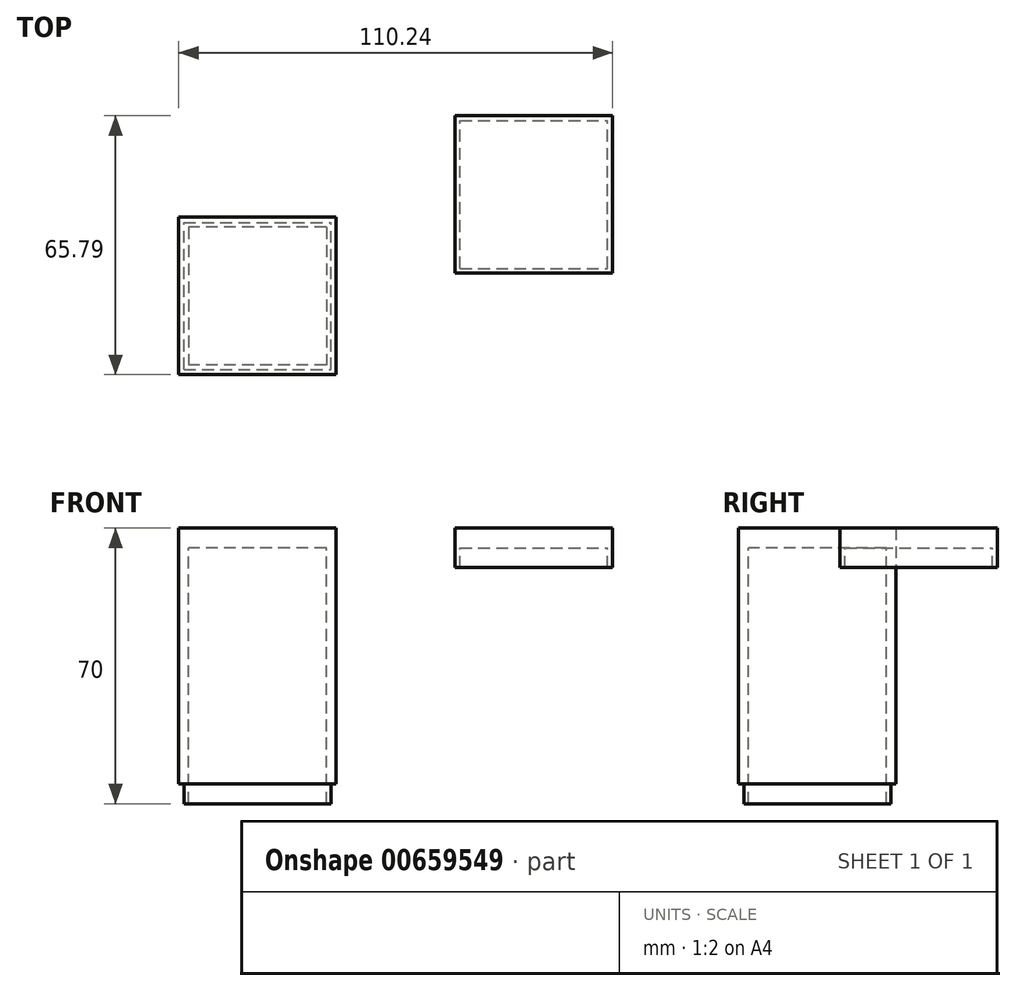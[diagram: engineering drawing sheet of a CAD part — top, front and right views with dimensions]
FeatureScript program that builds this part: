
annotation { "Feature Type Name" : "Feature", "Feature Type Description" : "" }
export const myFeature = defineFeature(function(context is Context, id is Id, definition is map)
    precondition{}
    {
        {
            var Q0;
            Q0=qCreatedBy(makeId("Top.planeOp"),FACE);
            var sketch = newSketch(context, id + "F0", { "sketchPlane" : qUnion([Q0])});
            skLineSegment(sketch, "E0.bottom", {"start": v(-20, -20) * mm, "end": v(20, -20) * mm});
            skLineSegment(sketch, "E0.top", {"start": v(-20, 20) * mm, "end": v(20, 20) * mm});
            skLineSegment(sketch, "E0.left", {"start": v(-20, -20) * mm, "end": v(-20, 20) * mm});
            skLineSegment(sketch, "E0.right", {"start": v(20, -20) * mm, "end": v(20, 20) * mm});
            skPoint(sketch, "E0.middle", {"position": v(0, 0) * mm});
            skSolve(sketch);
        }
        {
            var Q0;
            Q0=makeQuery(id+"F0.imprint","IMPRINT",FACE,{"disambiguationData":[TD([[makeQuery(id+"F0.imprint","IMPRINT",EDGE,{"derivedFrom":sQuery(id+"F0.wireOp",EDGE,"E0.bottom")}),1.0]])]});
            extrude(context, id + "F1", {"entities" : qUnion([Q0]), "depth" : 5 * mm, "offsetDistance" : 25 * mm});
        }
        {
            var Q0;
            Q0=makeQuery(id+"F1.opExtrude","CAP_FACE",FACE,{"disambiguationData":[OSD([sQuery(id+"F0.wireOp",EDGE,"E0.bottom"),sQuery(id+"F0.wireOp",EDGE,"E0.top"),sQuery(id+"F0.wireOp",EDGE,"E0.left"),sQuery(id+"F0.wireOp",EDGE,"E0.right")])],"isStart":true});
            var sketch = newSketch(context, id + "F2", { "sketchPlane" : qUnion([Q0])});
            skLineSegment(sketch, "E1.bottom", {"start": v(17.5, -17.5) * mm, "end": v(-17.5, -17.5) * mm});
            skLineSegment(sketch, "E1.top", {"start": v(17.5, 17.5) * mm, "end": v(-17.5, 17.5) * mm});
            skLineSegment(sketch, "E1.left", {"start": v(17.5, -17.5) * mm, "end": v(17.5, 17.5) * mm});
            skLineSegment(sketch, "E1.right", {"start": v(-17.5, -17.5) * mm, "end": v(-17.5, 17.5) * mm});
            skPoint(sketch, "E1.middle", {"position": v(0, 0) * mm});
            skSolve(sketch);
        }
        {
            var Q0;
            Q0=makeQuery(id+"F2.imprint","IMPRINT",FACE,{"disambiguationData":[TD([[makeQuery(id+"F2.imprint","IMPRINT",EDGE,{"derivedFrom":sQuery(id+"F2.wireOp",EDGE,"E1.bottom")}),1.0]])]});
            extrude(context, id + "F3", {"entities" : qUnion([Q0]), "operationType" : NewBodyOperationType.ADD, "depth" : 60 * mm, "offsetDistance" : 25 * mm});
        }
        {
            var Q0;
            Q0=makeQuery(id+"F3.opExtrude","CAP_FACE",FACE,{"disambiguationData":[OSD([sQuery(id+"F0.wireOp",EDGE,"E0.bottom"),sQuery(id+"F0.wireOp",EDGE,"E0.top"),sQuery(id+"F0.wireOp",EDGE,"E0.left"),sQuery(id+"F0.wireOp",EDGE,"E0.right"),sQuery(id+"F2.wireOp",EDGE,"E1.bottom"),sQuery(id+"F2.wireOp",EDGE,"E1.top"),sQuery(id+"F2.wireOp",EDGE,"E1.left"),sQuery(id+"F2.wireOp",EDGE,"E1.right")])],"isStart":false});
            var sketch = newSketch(context, id + "F4", { "sketchPlane" : qUnion([Q0])});
            skLineSegment(sketch, "E2.bottom", {"start": v(-18.65, 18.65) * mm, "end": v(18.65, 18.65) * mm});
            skLineSegment(sketch, "E2.top", {"start": v(-18.65, -18.65) * mm, "end": v(18.65, -18.65) * mm});
            skLineSegment(sketch, "E2.left", {"start": v(-18.65, 18.65) * mm, "end": v(-18.65, -18.65) * mm});
            skLineSegment(sketch, "E2.right", {"start": v(18.65, 18.65) * mm, "end": v(18.65, -18.65) * mm});
            skPoint(sketch, "E2.middle", {"position": v(0, 0) * mm});
            skSolve(sketch);
        }
        {
            var Q0;
            Q0=makeQuery(id+"F4.imprint","IMPRINT",FACE,{"disambiguationData":[TD([[makeQuery(id+"F4.imprint","IMPRINT",EDGE,{"derivedFrom":sQuery(id+"F4.wireOp",EDGE,"E2.bottom")}),-1.0]])]});
            extrude(context, id + "F5", {"entities" : qUnion([Q0]), "operationType" : NewBodyOperationType.ADD, "depth" : 5 * mm, "offsetDistance" : 25 * mm});
        }
        {
            var Q0;
            Q0=qCreatedBy(makeId("Top.planeOp"),FACE);
            var sketch = newSketch(context, id + "F6", { "sketchPlane" : qUnion([Q0])});
            skLineSegment(sketch, "E3.bottom", {"start": v(50.24, 5.79) * mm, "end": v(90.24, 5.79) * mm});
            skLineSegment(sketch, "E3.top", {"start": v(50.24, 45.79) * mm, "end": v(90.24, 45.79) * mm});
            skLineSegment(sketch, "E3.left", {"start": v(50.24, 5.79) * mm, "end": v(50.24, 45.79) * mm});
            skLineSegment(sketch, "E3.right", {"start": v(90.24, 5.79) * mm, "end": v(90.24, 45.79) * mm});
            skPoint(sketch, "E3.middle", {"position": v(70.24, 25.79) * mm});
            skLineSegment(sketch, "E4.bottom", {"start": v(51.49, 7.04) * mm, "end": v(88.99, 7.04) * mm});
            skLineSegment(sketch, "E4.top", {"start": v(51.49, 44.54) * mm, "end": v(88.99, 44.54) * mm});
            skLineSegment(sketch, "E4.left", {"start": v(51.49, 7.04) * mm, "end": v(51.49, 44.54) * mm});
            skLineSegment(sketch, "E4.right", {"start": v(88.99, 7.04) * mm, "end": v(88.99, 44.54) * mm});
            skSolve(sketch);
        }
        {
            var Q0;
            Q0=makeQuery(id+"F6.imprint","IMPRINT",FACE,{"disambiguationData":[TD([[makeQuery(id+"F6.imprint","IMPRINT",EDGE,{"derivedFrom":sQuery(id+"F6.wireOp",EDGE,"E4.bottom")}),1.0]])]});
            var Q1;
            Q1=makeQuery(id+"F6.imprint","IMPRINT",FACE,{"disambiguationData":[TD([[makeQuery(id+"F6.imprint","IMPRINT",EDGE,{"derivedFrom":sQuery(id+"F6.wireOp",EDGE,"E3.bottom")}),1.0]])]});
            extrude(context, id + "F7", {"entities" : qUnion([Q0, Q1]), "depth" : 5 * mm, "offsetDistance" : 25 * mm});
        }
        {
            var Q0;
            Q0=makeQuery(id+"F6.imprint","IMPRINT",FACE,{"disambiguationData":[TD([[makeQuery(id+"F6.imprint","IMPRINT",EDGE,{"derivedFrom":sQuery(id+"F6.wireOp",EDGE,"E3.bottom")}),1.0]])]});
            extrude(context, id + "F8", {"entities" : qUnion([Q0]), "operationType" : NewBodyOperationType.ADD, "oppositeDirection" : true, "depth" : 5 * mm, "offsetDistance" : 25 * mm});
        }
    });
